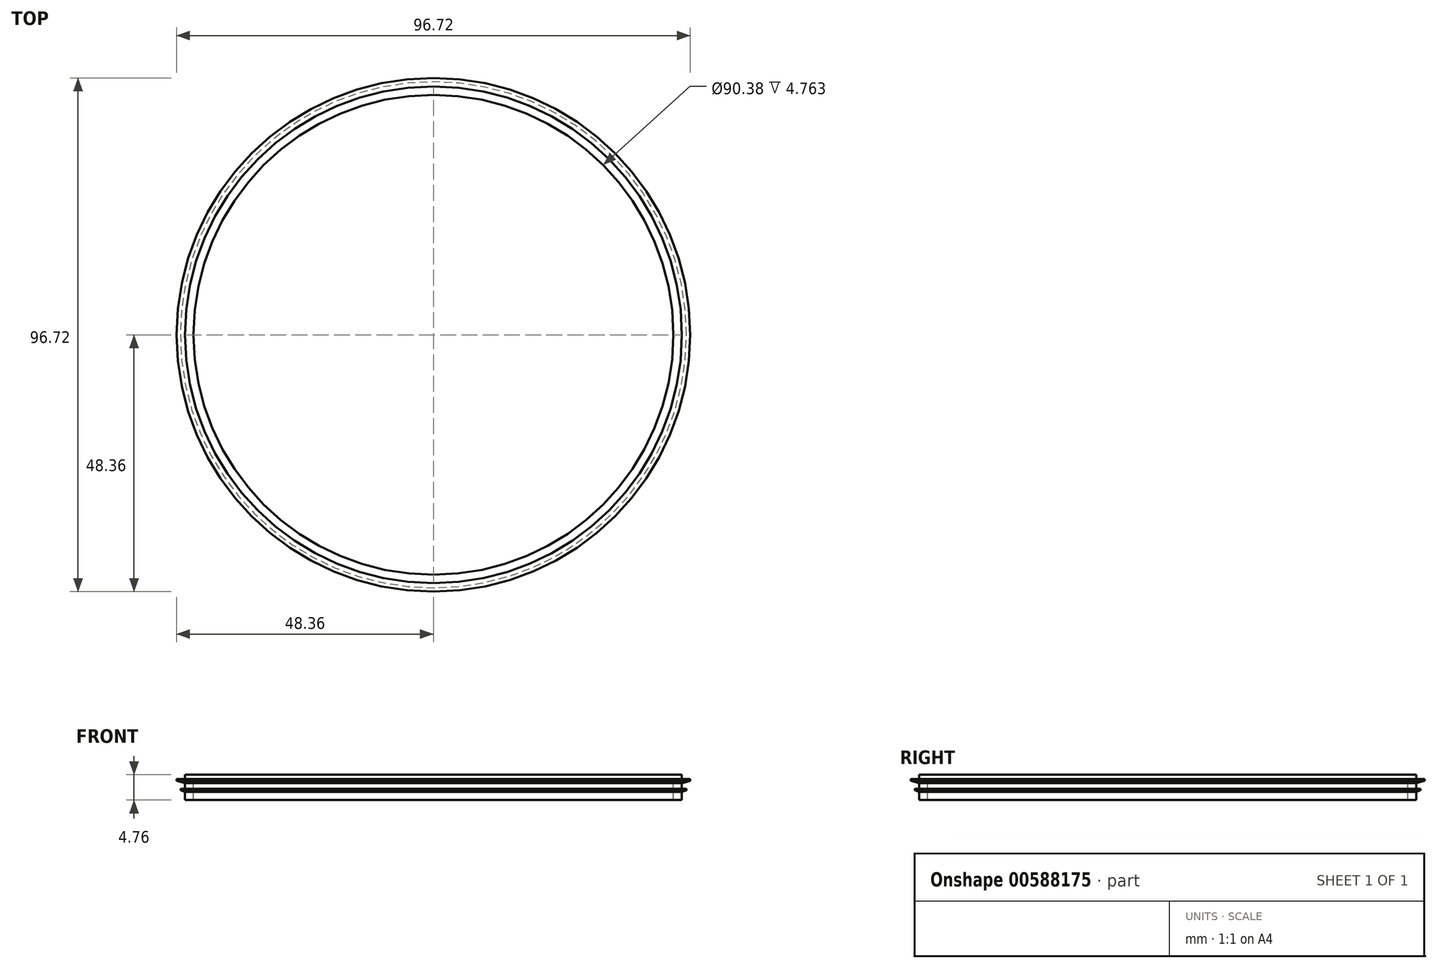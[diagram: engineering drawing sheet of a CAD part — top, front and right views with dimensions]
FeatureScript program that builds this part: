
annotation { "Feature Type Name" : "Feature", "Feature Type Description" : "" }
export const myFeature = defineFeature(function(context is Context, id is Id, definition is map)
    precondition{}
    {
        {
            var Q0;
            Q0=qCreatedBy(makeId("Front.planeOp"),FACE);
            var sketch = newSketch(context, id + "F0", { "sketchPlane" : qUnion([Q0])});
            skLineSegment(sketch, "E0", {"start": v(0, 0) * mm, "end": v(45.19, 0) * mm});
            skLineSegment(sketch, "E1", {"start": v(45.19, 0) * mm, "end": v(46.78, 0) * mm});
            skLineSegment(sketch, "E2", {"start": v(46.78, 0) * mm, "end": v(46.78, -0.8) * mm});
            skLineSegment(sketch, "E3", {"start": v(46.78, -4.76) * mm, "end": v(45.19, -4.76) * mm});
            skLineSegment(sketch, "E4", {"start": v(45.19, -4.76) * mm, "end": v(45.19, 0) * mm});
            skLineSegment(sketch, "E5", {"start": v(46.78, -0.8) * mm, "end": v(48.36, -0.8) * mm});
            skLineSegment(sketch, "E6", {"start": v(48.36, -0.8) * mm, "end": v(48.36, -1.13) * mm});
            skLineSegment(sketch, "E7", {"start": v(48.36, -1.13) * mm, "end": v(46.78, -1.59) * mm});
            skLineSegment(sketch, "E8.trimOffspring", {"start": v(46.78, -1.59) * mm, "end": v(46.78, -2.65) * mm});
            skLineSegment(sketch, "E9", {"start": v(46.78, -2.65) * mm, "end": v(47.63, -2.65) * mm});
            skLineSegment(sketch, "E10", {"start": v(47.63, -2.65) * mm, "end": v(47.63, -2.92) * mm});
            skLineSegment(sketch, "E11", {"start": v(47.63, -2.92) * mm, "end": v(46.78, -3.19) * mm});
            skPoint(sketch, "E12.start.orphan", {"position": v(47.63, -3.19) * mm});
            skLineSegment(sketch, "E13.trimOffspring", {"start": v(46.78, -3.19) * mm, "end": v(46.78, -4.76) * mm});
            skLineSegment(sketch, "E14", {"start": v(0, 0) * mm, "end": v(0, -8.03) * mm});
            skSolve(sketch);
        }
        {
            var Q0;
            Q0 = qSketchRegion(id + "F0", true);
            var Q1;
            Q1=sQuery(id+"F0.wireOp",EDGE,"E14");
            revolve(context, id + "F1", {"entities" : qUnion([Q0]), "axis" : qUnion([Q1]), "revolveType" : RevolveType.FULL});
        }
    });
